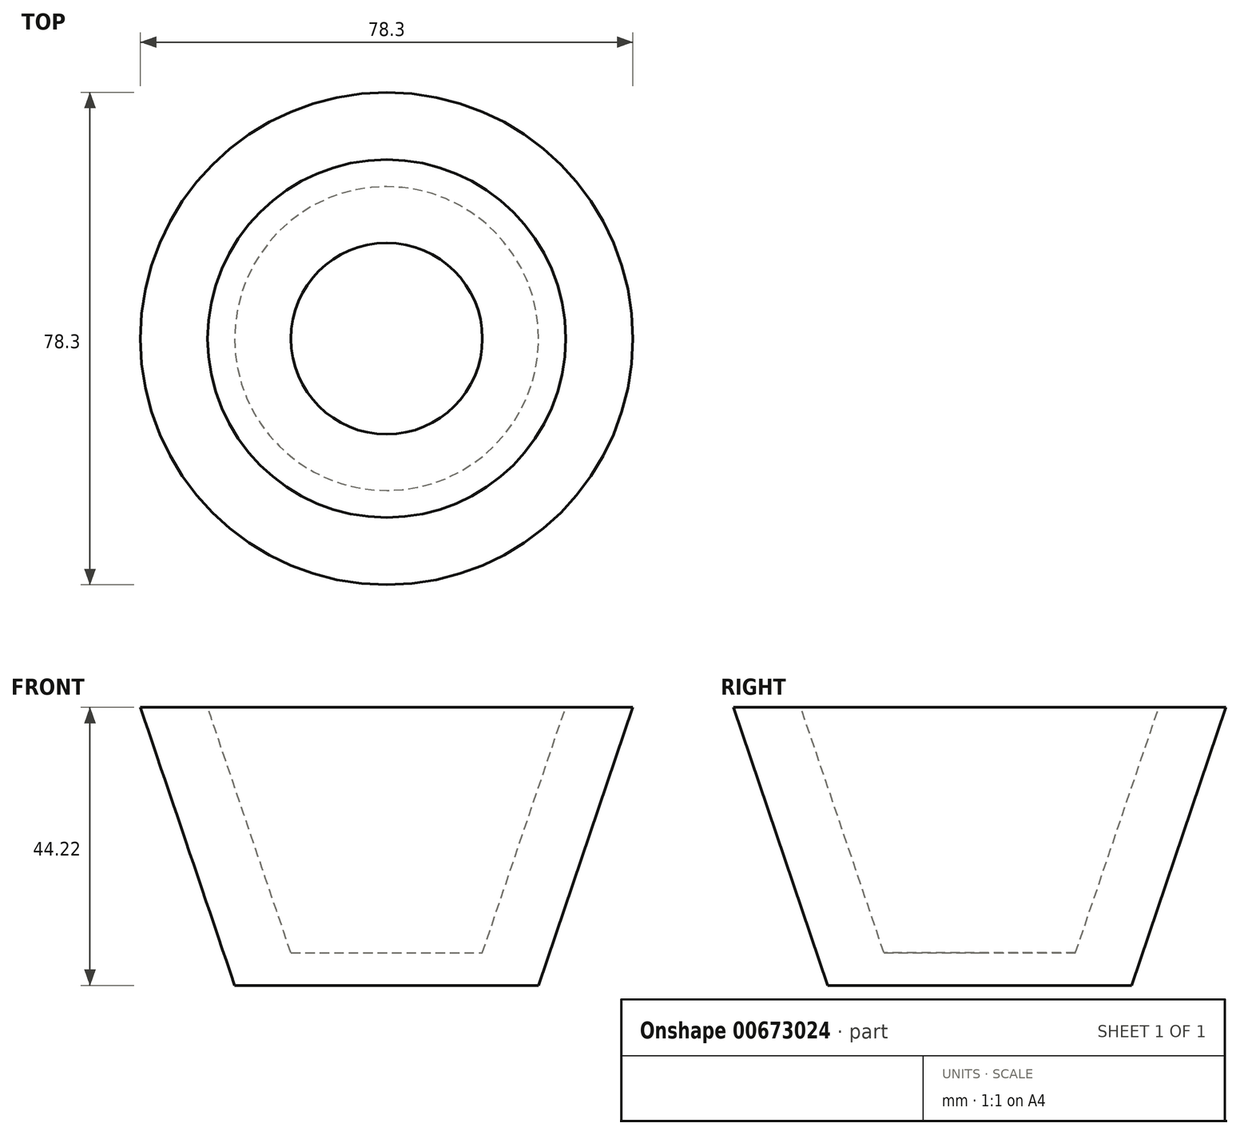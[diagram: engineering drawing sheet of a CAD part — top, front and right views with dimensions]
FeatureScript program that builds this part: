
annotation { "Feature Type Name" : "Feature", "Feature Type Description" : "" }
export const myFeature = defineFeature(function(context is Context, id is Id, definition is map)
    precondition{}
    {
        {
            var Q0;
            Q0=qCreatedBy(makeId("Front.planeOp"),FACE);
            var sketch = newSketch(context, id + "F0", { "sketchPlane" : qUnion([Q0])});
            skLineSegment(sketch, "E0", {"start": v(-81.32, 31.65) * mm, "end": v(-66.1, 31.65) * mm});
            skLineSegment(sketch, "E1", {"start": v(-66.1, 31.65) * mm, "end": v(-52.86, 70.7) * mm});
            skLineSegment(sketch, "E2", {"start": v(-52.86, 70.7) * mm, "end": v(-42.17, 70.7) * mm});
            skLineSegment(sketch, "E3", {"start": v(-42.17, 70.7) * mm, "end": v(-57.17, 26.48) * mm});
            skLineSegment(sketch, "E4", {"start": v(-57.17, 26.48) * mm, "end": v(-81.32, 26.48) * mm});
            skLineSegment(sketch, "E5", {"start": v(-81.32, 26.48) * mm, "end": v(-81.32, 31.65) * mm});
            skSolve(sketch);
        }
        {
            var Q0;
            Q0 = qSketchRegion(id + "F0", true);
            var Q1;
            Q1=sQuery(id+"F0.wireOp",EDGE,"E5");
            revolve(context, id + "F1", {"entities" : qUnion([Q0]), "axis" : qUnion([Q1]), "revolveType" : RevolveType.FULL});
        }
    });
